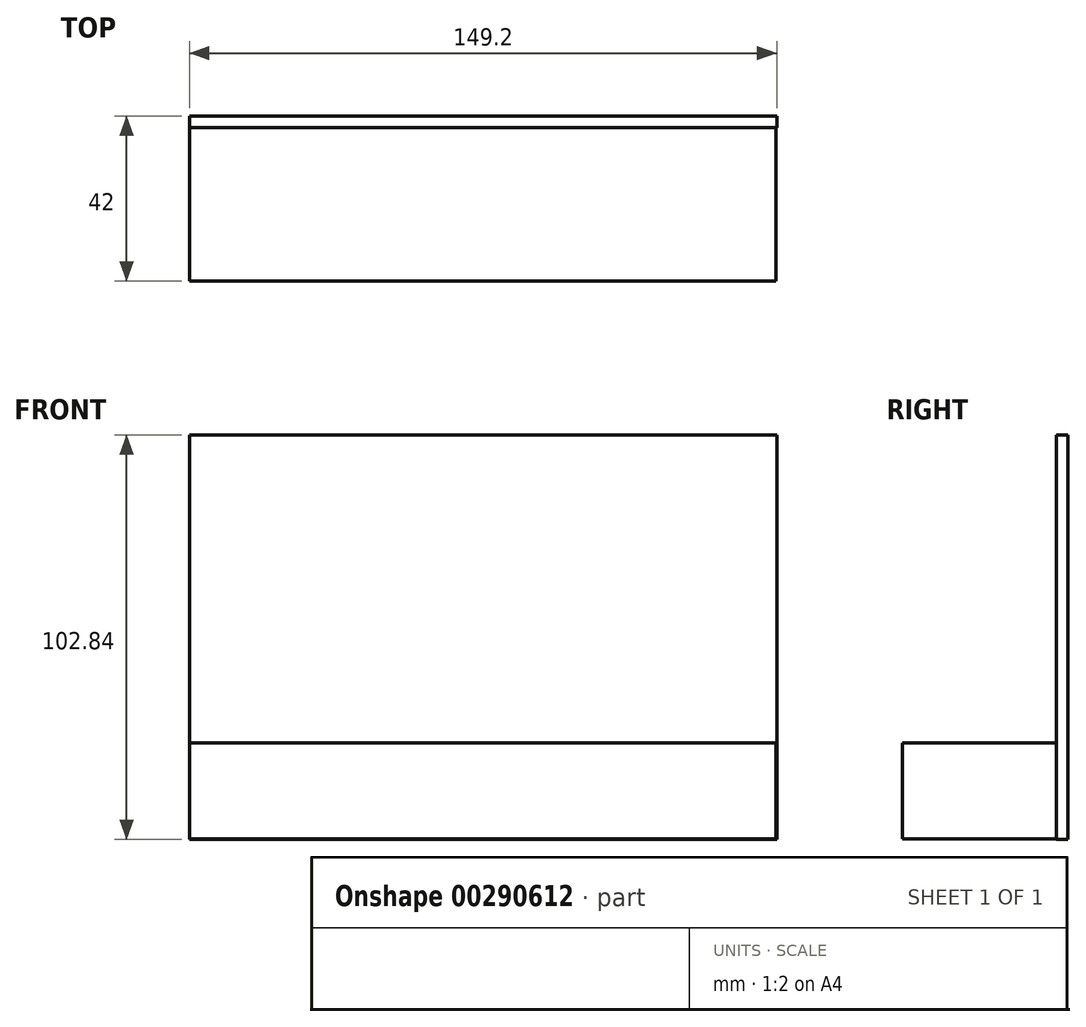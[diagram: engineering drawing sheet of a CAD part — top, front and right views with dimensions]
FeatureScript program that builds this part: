
annotation { "Feature Type Name" : "Feature", "Feature Type Description" : "" }
export const myFeature = defineFeature(function(context is Context, id is Id, definition is map)
    precondition{}
    {
        {
            var Q0;
            Q0=qCreatedBy(makeId("Front.planeOp"),FACE);
            var sketch = newSketch(context, id + "F0", { "sketchPlane" : qUnion([Q0])});
            skLineSegment(sketch, "E0.bottom", {"start": v(74.6, 51.42) * mm, "end": v(-74.6, 51.42) * mm});
            skLineSegment(sketch, "E0.top", {"start": v(74.6, -51.42) * mm, "end": v(-74.6, -51.42) * mm});
            skLineSegment(sketch, "E0.left", {"start": v(74.6, 51.42) * mm, "end": v(74.6, -51.42) * mm});
            skLineSegment(sketch, "E0.right", {"start": v(-74.6, 51.42) * mm, "end": v(-74.6, -51.42) * mm});
            skPoint(sketch, "E0.middle", {"position": v(0, 0) * mm});
            skSolve(sketch);
        }
        {
            var Q0;
            Q0 = qSketchRegion(id + "F0", true);
            extrude(context, id + "F1", {"entities" : qUnion([Q0]), "depth" : 3 * mm});
        }
        {
            var Q0;
            Q0=makeQuery(id+"F1.opExtrude","CAP_FACE",FACE,{"disambiguationData":[OSD([sQuery(id+"F0.wireOp",EDGE,"E0.bottom"),sQuery(id+"F0.wireOp",EDGE,"E0.top"),sQuery(id+"F0.wireOp",EDGE,"E0.left"),sQuery(id+"F0.wireOp",EDGE,"E0.right")])],"isStart":false});
            var sketch = newSketch(context, id + "F2", { "sketchPlane" : qUnion([Q0])});
            skLineSegment(sketch, "E1.bottom", {"start": v(-74.79, -51.23) * mm, "end": v(74.42, -51.23) * mm});
            skLineSegment(sketch, "E1.top", {"start": v(-74.79, -26.85) * mm, "end": v(74.42, -26.85) * mm});
            skLineSegment(sketch, "E1.left", {"start": v(-74.79, -51.23) * mm, "end": v(-74.79, -26.85) * mm});
            skLineSegment(sketch, "E1.right", {"start": v(74.42, -51.23) * mm, "end": v(74.42, -26.85) * mm});
            skSolve(sketch);
        }
        {
            var Q0;
            {var subQ0=sQuery(id+"F2.wireOp",EDGE,"E1.right");Q0=makeQuery(id+"F2.imprint","IMPRINT",FACE,{"disambiguationData":[TD([[makeQuery(id+"F2.imprint","IMPRINT",EDGE,{"derivedFrom":subQ0}),1.0]])]});}
            extrude(context, id + "F3", {"entities" : qUnion([Q0]), "depth" : 39 * mm});
        }
        {
            var Q0;
            Q0=makeQuery(id+"F3.opExtrude","SWEPT_FACE",FACE,{"disambiguationData":[OSD([sQuery(id+"F0.wireOp",EDGE,"E0.right")])]});
            cPlane(context, id + "F4", {"entities" : qUnion([Q0]), "cplaneType" : CPlaneType.OFFSET, "offset" : 14.2 * mm, "oppositeDirection" : true, "width" : 150 * mm, "height" : 150 * mm});
        }
    });
